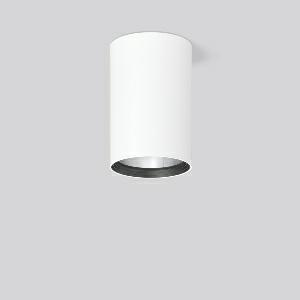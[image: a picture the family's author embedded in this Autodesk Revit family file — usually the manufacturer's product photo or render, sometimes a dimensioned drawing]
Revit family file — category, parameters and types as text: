
# Revit family: heledon_maxi_a_931217_002_3_76_4c89
name_source: partatom
category: Lighting Fixtures
units: mm (PartAtom-declared; Revit-internal decimal feet)

## family parameters
Cut with Voids When Loaded = No
Host = Face
Light Source = No
Part Type = Normal
Room Calculation Point = No
Round Connector Dimension = Use Diameter
Shared = No

## types (1)
- HELEDON maxi A (1 x LED Modul 935, 3400 lm, 3500)
    Apparent Load = 25 VA
    Approval mark = CE
    CIE Flux Codes = 100 100 100 100 100
    Color Rendering = 92
    Color Temperature = 3500
    Default Elevation = 1800 mm
    Description = Series: HELEDON maxi
Cylindrical surface-mounted downlight. Housing: die-cast aluminium, powder-coated. Internal ceiling frame polycarbonate with bayonet mounting. Black plastic ring and recessed LED to prevent glare from the side. Optical assembly with reflector made of MIRO-Silver with 98% total light reflection for outstanding efficiency - can be changed without tools. Best colour rendering index Ra>90. Suitable for Ceiling mounting. Easy installation with a separate ceiling frame with bayonet mounting and plug connection. Driver integrated. Connected via plug-in connector. High quality converter without flickering and stroboscopic effect. The following accessories can be mounted without use of tools: interchangeable lenses, decorative glasses, honeycomb louvre, clear and frosted diffusers, white interchangeable plastic ring. 
Colour: traffic white, matt (RAL 9016)
Diameter: 123 mm
Height: 183 mm
Lamp: LED
Socket: without socket
Colour temperature: 3500K
Colour rendering index (CRI): 92
System power: 25 W
Rated luminous flux: 3400 lm
Luminous efficiency: 136 lm/W
Control gear: Converter, dimmable, DALI
Protection class: I
Type of protection: IP 20
    Height = 183 mm
    Lamp = 1 x LED Modul 935
    Lamp Light Flux = 3400 lm
    Lamp count = 1
    Length = 123 mm
    Lifetime = 50000 h
    Luminous efficacy = 136 lm/W
    Manufacturer = RZB
    ModVariant = No
    Model = 931217.002.3.76
    Mounting Place = Ceiling
    Mounting Type = Surface mounted
    Number of Poles = 1
    OnlyDefault = Yes
    Power Factor = 1
    Product Name = HELEDON maxi A
    Product group = Surface mounted downlights
    ProductGroupID = 302
    Protection Class = Protection class I
    Protection Degree = IP 20
    RLX_Detail_Level = 1
    RLX_Emergency_Light_Flux = 0 lm
    RLX_Emergency_Type = 0
    RLX_Emergency_Type_DB = No
    RlxData = <blob elided: 98601 chars, md5=2f307270>
    Socket = socket
    Standby Power = 0 W
    System Light Flux = 3400 lm
    System Power = 25 W
    Type Comments = Product without accessories
    Type Image = 931192.002.jpg
    URL = http://relux.com
    VarID = ---
    Voltage = 230 V
    Voltage Range = 220-240 V
    Weight = 0.00 kg
    Width = 0 mm  [stored 0 ft]

note: [stored X ft] marks values corroborated as IEEE doubles in the binary element streams (Revit-internal decimal feet)

## geometry (parser evidence)
native form markers: Blend x4, Sweep x10
no freeform markers — native parametric forms only
